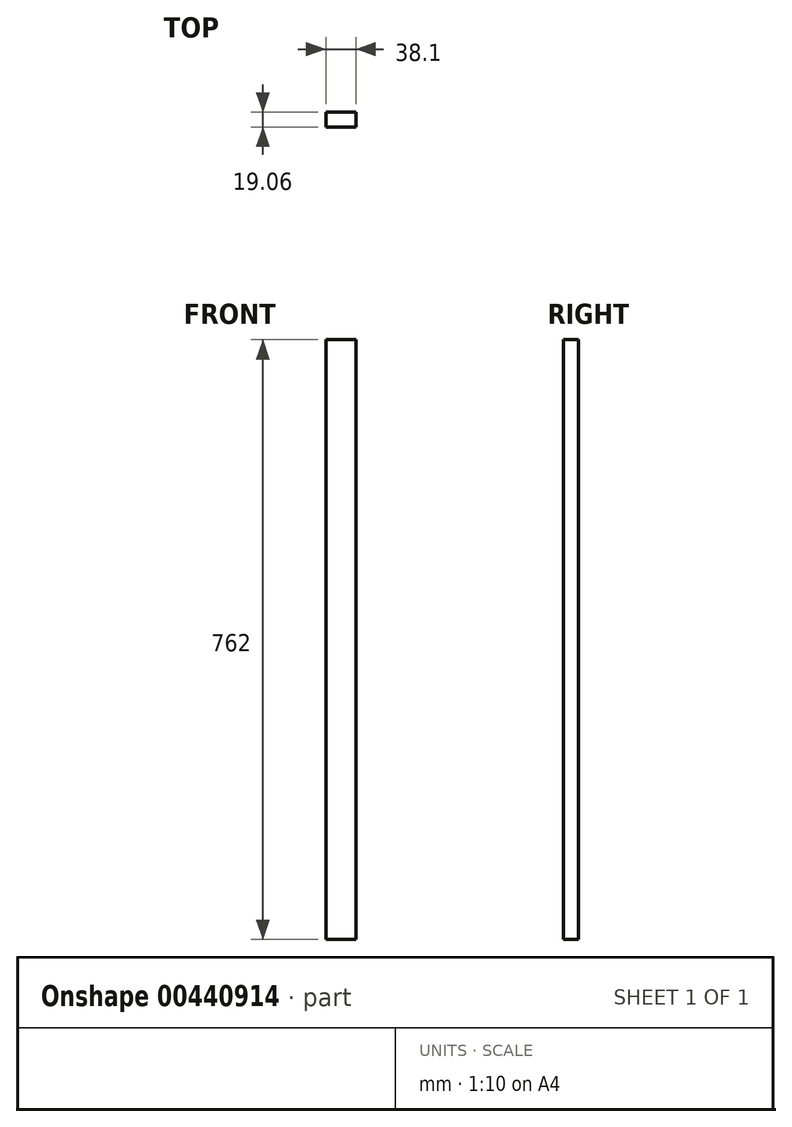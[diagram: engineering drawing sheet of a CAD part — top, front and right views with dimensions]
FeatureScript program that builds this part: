
annotation { "Feature Type Name" : "Feature", "Feature Type Description" : "" }
export const myFeature = defineFeature(function(context is Context, id is Id, definition is map)
    precondition{}
    {
        {
            var Q0;
            Q0=qCreatedBy(makeId("Top.planeOp"),FACE);
            var sketch = newSketch(context, id + "F0", { "sketchPlane" : qUnion([Q0])});
            skLineSegment(sketch, "E0.bottom", {"start": v(19.05, 9.52) * mm, "end": v(-19.05, 9.52) * mm});
            skLineSegment(sketch, "E0.top", {"start": v(19.05, -9.53) * mm, "end": v(-19.05, -9.53) * mm});
            skLineSegment(sketch, "E0.left", {"start": v(19.05, 9.53) * mm, "end": v(19.05, -9.53) * mm});
            skLineSegment(sketch, "E0.right", {"start": v(-19.05, 9.53) * mm, "end": v(-19.05, -9.53) * mm});
            skPoint(sketch, "E0.middle", {"position": v(0, 0) * mm});
            skSolve(sketch);
        }
        {
            var Q0;
            Q0 = qSketchRegion(id + "F0", true);
            extrude(context, id + "F1", {"entities" : qUnion([Q0]), "depth" : 762 * mm});
        }
    });
